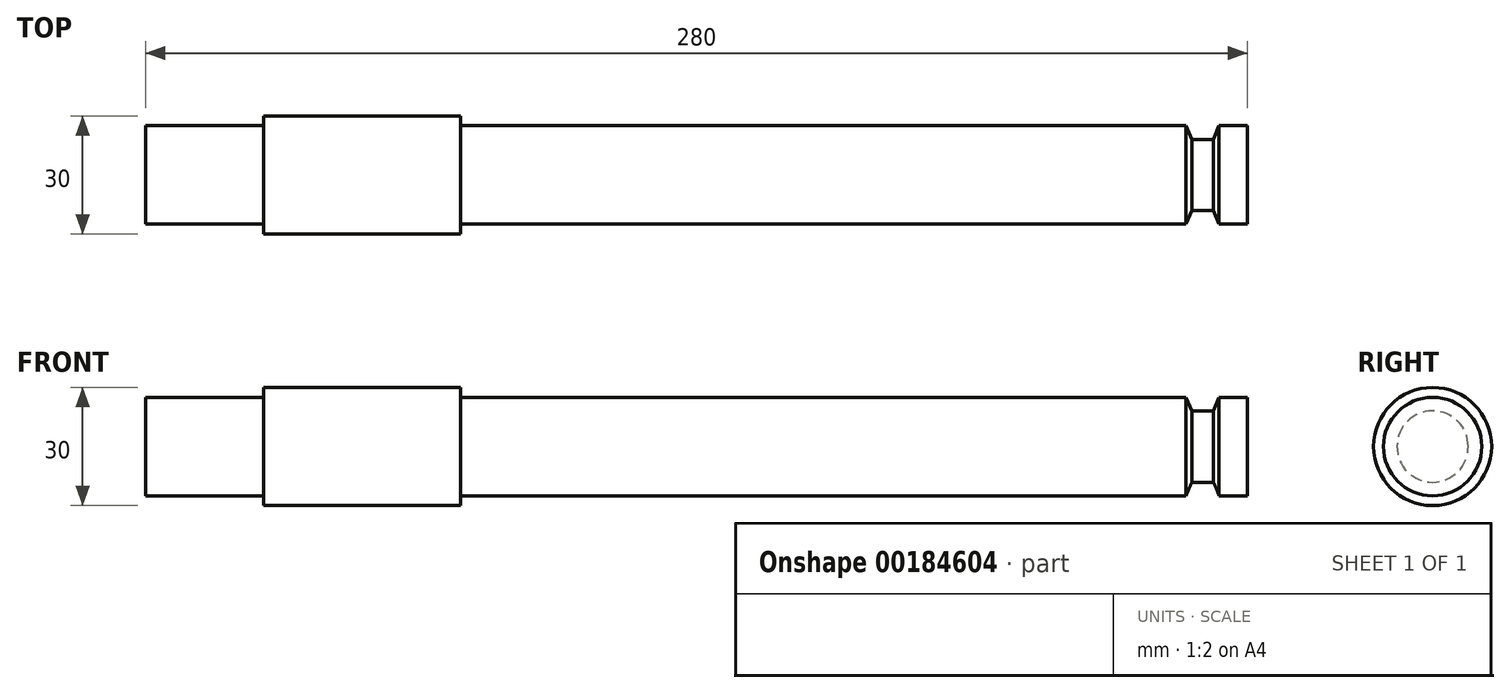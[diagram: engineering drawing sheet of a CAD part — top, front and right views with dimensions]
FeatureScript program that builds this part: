
annotation { "Feature Type Name" : "Feature", "Feature Type Description" : "" }
export const myFeature = defineFeature(function(context is Context, id is Id, definition is map)
    precondition{}
    {
        {
            var Q0;
            Q0=qCreatedBy(makeId("Front.planeOp"),FACE);
            var sketch = newSketch(context, id + "F0", { "sketchPlane" : qUnion([Q0])});
            skLineSegment(sketch, "E0", {"start": v(-71.36, 0) * mm, "end": v(-71.36, -12.5) * mm});
            skLineSegment(sketch, "E1", {"start": v(-71.36, -12.5) * mm, "end": v(-41.36, -12.5) * mm});
            skLineSegment(sketch, "E2", {"start": v(-41.36, -12.5) * mm, "end": v(-41.36, -15) * mm});
            skLineSegment(sketch, "E3", {"start": v(-41.36, -15) * mm, "end": v(8.64, -15) * mm});
            skLineSegment(sketch, "E4", {"start": v(8.64, -15) * mm, "end": v(8.64, -12.5) * mm});
            skLineSegment(sketch, "E5", {"start": v(8.64, -12.5) * mm, "end": v(208.64, -12.5) * mm});
            skLineSegment(sketch, "E6", {"start": v(208.64, -12.5) * mm, "end": v(208.64, 0) * mm});
            skLineSegment(sketch, "E7", {"start": v(208.64, 0) * mm, "end": v(-71.36, 0) * mm});
            skLineSegment(sketch, "E8", {"start": v(192.99, -12.5) * mm, "end": v(194.43, -9.06) * mm});
            skLineSegment(sketch, "E9", {"start": v(194.43, -9.06) * mm, "end": v(199.97, -9.06) * mm});
            skLineSegment(sketch, "E10", {"start": v(199.97, -9.06) * mm, "end": v(201.4, -12.5) * mm});
            skLineSegment(sketch, "E11", {"start": v(201.4, -12.5) * mm, "end": v(192.99, -12.5) * mm});
            skSolve(sketch);
        }
        {
            var Q0;
            Q0=makeQuery(id+"F0.imprint","IMPRINT",FACE,{"disambiguationData":[TD([[makeQuery(id+"F0.imprint","IMPRINT",EDGE,{"derivedFrom":sQuery(id+"F0.wireOp",EDGE,"E0")}),1.0]])]});
            var Q1;
            Q1=sQuery(id+"F0.wireOp",EDGE,"E7");
            revolve(context, id + "F1", {"entities" : qUnion([Q0]), "axis" : qUnion([Q1]), "revolveType" : RevolveType.FULL});
        }
    });
